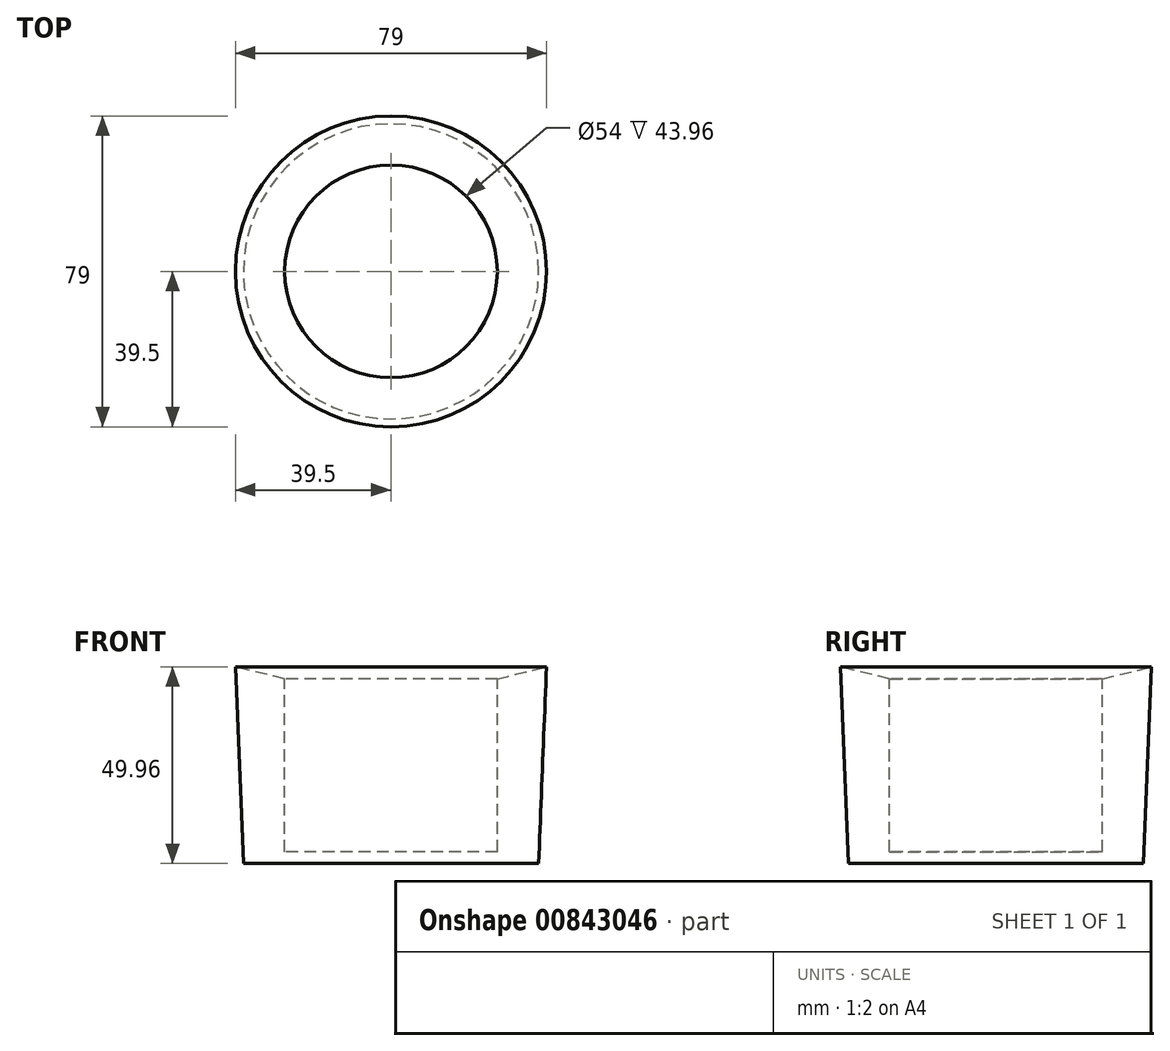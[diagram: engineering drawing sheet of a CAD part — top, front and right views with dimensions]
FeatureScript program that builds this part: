
annotation { "Feature Type Name" : "Feature", "Feature Type Description" : "" }
export const myFeature = defineFeature(function(context is Context, id is Id, definition is map)
    precondition{}
    {
        {
            var Q0;
            Q0=qCreatedBy(makeId("Right.planeOp"),FACE);
            var sketch = newSketch(context, id + "F0", { "sketchPlane" : qUnion([Q0])});
            skLineSegment(sketch, "E0", {"start": v(-39.5, 49.96) * mm, "end": v(-27, 46.96) * mm});
            skLineSegment(sketch, "E1", {"start": v(-27, 46.96) * mm, "end": v(-27, 3) * mm});
            skLineSegment(sketch, "E2", {"start": v(-27, 3) * mm, "end": v(0, 3) * mm});
            skLineSegment(sketch, "E3", {"start": v(0, 3) * mm, "end": v(0, 0) * mm});
            skLineSegment(sketch, "E4", {"start": v(0, 0) * mm, "end": v(-37.5, 0) * mm});
            skLineSegment(sketch, "E5", {"start": v(-37.5, 0) * mm, "end": v(-39.5, 49.96) * mm});
            skSolve(sketch);
        }
        {
            var Q0;
            Q0=makeQuery(id+"F0.imprint","IMPRINT",FACE,{"disambiguationData":[TD([[makeQuery(id+"F0.imprint","IMPRINT",EDGE,{"derivedFrom":sQuery(id+"F0.wireOp",EDGE,"E0")}),-1.0]])]});
            var Q1;
            Q1=sQuery(id+"F0.wireOp",EDGE,"E3");
            revolve(context, id + "F1", {"surfaceOperationType" : NewSurfaceOperationType.NEW, "entities" : qUnion([Q0]), "axis" : qUnion([Q1]), "revolveType" : RevolveType.FULL});
        }
    });
